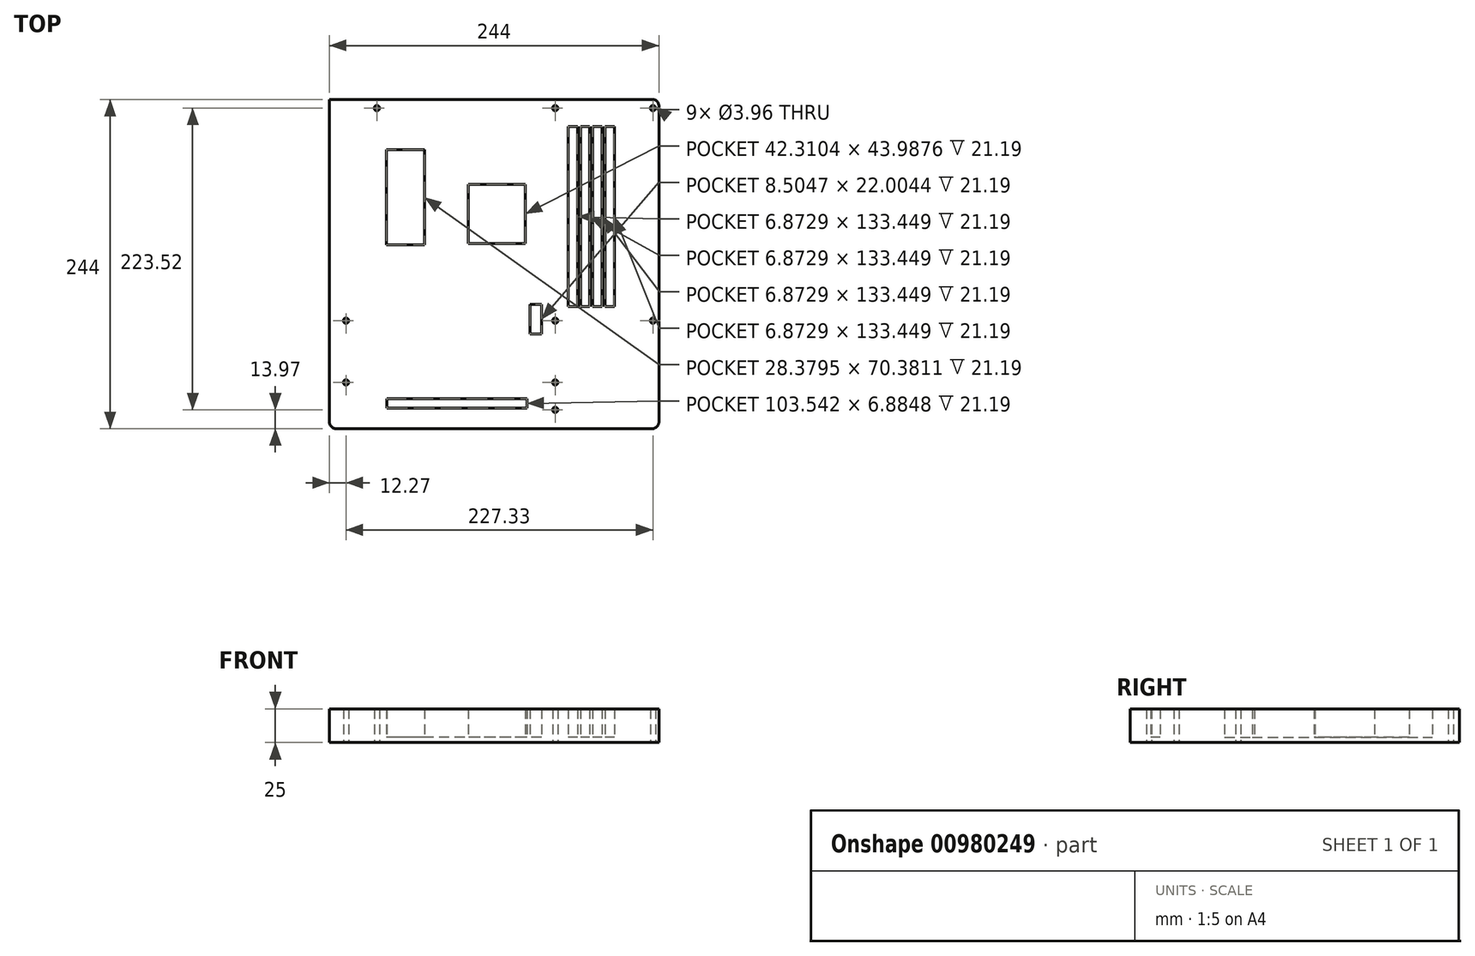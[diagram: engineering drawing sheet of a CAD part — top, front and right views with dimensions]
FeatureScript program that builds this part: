
annotation { "Feature Type Name" : "Feature", "Feature Type Description" : "" }
export const myFeature = defineFeature(function(context is Context, id is Id, definition is map)
    precondition{}
    {
        {
            var Q0;
            Q0=qCreatedBy(makeId("Top.planeOp"),FACE);
            var sketch = newSketch(context, id + "F0", { "sketchPlane" : qUnion([Q0])});
            skLineSegment(sketch, "E0.bottom", {"start": v(5, 0) * mm, "end": v(239, 0) * mm});
            skLineSegment(sketch, "E0.top", {"start": v(0, 244) * mm, "end": v(239, 244) * mm});
            skLineSegment(sketch, "E0.left", {"start": v(0, 5) * mm, "end": v(0, 244) * mm});
            skLineSegment(sketch, "E0.right", {"start": v(244, 5) * mm, "end": v(244, 239) * mm});
            skCircle(sketch, "E1", {"center": v(35.13, 237.49) * mm, "radius": 1.98 * mm});
            skCircle(sketch, "E2", {"center": v(167.2, 237.49) * mm, "radius": 1.98 * mm});
            skCircle(sketch, "E3", {"center": v(239.6, 237.49) * mm, "radius": 1.98 * mm});
            skCircle(sketch, "E4", {"center": v(12.27, 80) * mm, "radius": 1.98 * mm});
            skCircle(sketch, "E5", {"center": v(167.21, 80) * mm, "radius": 1.98 * mm});
            skCircle(sketch, "E6", {"center": v(239.6, 80) * mm, "radius": 1.98 * mm});
            skCircle(sketch, "E7", {"center": v(12.27, 34.3) * mm, "radius": 1.98 * mm});
            skCircle(sketch, "E8", {"center": v(167.21, 34.29) * mm, "radius": 1.98 * mm});
            skCircle(sketch, "E9", {"center": v(167.21, 13.97) * mm, "radius": 1.98 * mm});
            skLineSegment(sketch, "E10.bottom", {"start": v(0, 244) * mm, "end": v(22.47, 244) * mm});
            skLineSegment(sketch, "E10.top", {"start": v(0, 85.25) * mm, "end": v(22.47, 85.25) * mm});
            skLineSegment(sketch, "E10.left", {"start": v(0, 244) * mm, "end": v(0, 85.25) * mm});
            skLineSegment(sketch, "E10.right", {"start": v(22.47, 244) * mm, "end": v(22.47, 85.25) * mm});
            skLineSegment(sketch, "E11.bottom", {"start": v(148.54, 92.04) * mm, "end": v(157.04, 92.04) * mm});
            skLineSegment(sketch, "E11.top", {"start": v(148.54, 70.03) * mm, "end": v(157.04, 70.03) * mm});
            skLineSegment(sketch, "E11.left", {"start": v(148.54, 92.04) * mm, "end": v(148.54, 70.03) * mm});
            skLineSegment(sketch, "E11.right", {"start": v(157.04, 92.04) * mm, "end": v(157.04, 70.03) * mm});
            skLineSegment(sketch, "E12.bottom", {"start": v(102.72, 137.02) * mm, "end": v(145.03, 137.02) * mm});
            skLineSegment(sketch, "E12.top", {"start": v(102.72, 181) * mm, "end": v(145.03, 181) * mm});
            skLineSegment(sketch, "E12.left", {"start": v(102.72, 137.02) * mm, "end": v(102.72, 181) * mm});
            skLineSegment(sketch, "E12.right", {"start": v(145.03, 137.02) * mm, "end": v(145.03, 181) * mm});
            skLineSegment(sketch, "E13.bottom", {"start": v(176.77, 223.94) * mm, "end": v(183.64, 223.94) * mm});
            skLineSegment(sketch, "E13.top", {"start": v(176.77, 90.5) * mm, "end": v(183.64, 90.5) * mm});
            skLineSegment(sketch, "E13.left", {"start": v(176.77, 223.94) * mm, "end": v(176.77, 90.5) * mm});
            skLineSegment(sketch, "E13.right", {"start": v(183.64, 223.94) * mm, "end": v(183.64, 90.5) * mm});
            skLineSegment(sketch, "E14.1.0.0", {"start": v(192.74, 223.94) * mm, "end": v(192.74, 90.5) * mm});
            skLineSegment(sketch, "E14.1.0.1", {"start": v(185.87, 223.94) * mm, "end": v(185.87, 90.5) * mm});
            skLineSegment(sketch, "E14.1.0.2", {"start": v(185.87, 90.5) * mm, "end": v(192.74, 90.5) * mm});
            skLineSegment(sketch, "E14.1.0.3", {"start": v(185.87, 223.94) * mm, "end": v(192.74, 223.94) * mm});
            skLineSegment(sketch, "E14.2.0.0", {"start": v(201.84, 223.94) * mm, "end": v(201.84, 90.5) * mm});
            skLineSegment(sketch, "E14.2.0.1", {"start": v(194.97, 223.94) * mm, "end": v(194.97, 90.5) * mm});
            skLineSegment(sketch, "E14.2.0.2", {"start": v(194.97, 90.5) * mm, "end": v(201.84, 90.5) * mm});
            skLineSegment(sketch, "E14.2.0.3", {"start": v(194.97, 223.94) * mm, "end": v(201.84, 223.94) * mm});
            skLineSegment(sketch, "E14.3.0.0", {"start": v(210.94, 223.94) * mm, "end": v(210.94, 90.5) * mm});
            skLineSegment(sketch, "E14.3.0.1", {"start": v(204.07, 223.94) * mm, "end": v(204.07, 90.5) * mm});
            skLineSegment(sketch, "E14.3.0.2", {"start": v(204.07, 90.5) * mm, "end": v(210.94, 90.5) * mm});
            skLineSegment(sketch, "E14.3.0.3", {"start": v(204.07, 223.94) * mm, "end": v(210.94, 223.94) * mm});
            skLineSegment(sketch, "E14.direction1", {"start": v(183.64, 90.5) * mm, "end": v(192.74, 90.5) * mm, "construction": true});
            skLineSegment(sketch, "E15.bottom", {"start": v(42.63, 15.38) * mm, "end": v(146.17, 15.38) * mm});
            skLineSegment(sketch, "E15.top", {"start": v(42.63, 22.27) * mm, "end": v(146.17, 22.27) * mm});
            skLineSegment(sketch, "E15.left", {"start": v(42.63, 15.38) * mm, "end": v(42.63, 22.27) * mm});
            skLineSegment(sketch, "E15.right", {"start": v(146.17, 15.38) * mm, "end": v(146.17, 22.27) * mm});
            skLineSegment(sketch, "E16.bottom", {"start": v(42.19, 136.37) * mm, "end": v(70.57, 136.37) * mm});
            skLineSegment(sketch, "E16.top", {"start": v(42.19, 206.75) * mm, "end": v(70.57, 206.75) * mm});
            skLineSegment(sketch, "E16.left", {"start": v(42.19, 136.37) * mm, "end": v(42.19, 206.75) * mm});
            skLineSegment(sketch, "E16.right", {"start": v(70.57, 136.37) * mm, "end": v(70.57, 206.75) * mm});
            skLineSegment(sketch, "E17.bottom", {"start": v(85.1, 221.74) * mm, "end": v(155.48, 221.74) * mm});
            skLineSegment(sketch, "E17.top", {"start": v(85.1, 244) * mm, "end": v(155.48, 244) * mm});
            skLineSegment(sketch, "E17.left", {"start": v(85.1, 221.74) * mm, "end": v(85.1, 244) * mm});
            skLineSegment(sketch, "E17.right", {"start": v(155.48, 221.74) * mm, "end": v(155.48, 244) * mm});
            skPoint(sketch, "E18.visualSharp", {"position": v(244, 0) * mm});
            skArc(sketch, "E18.filletArc", {"start": v(239, 0) * mm, "mid": v(242.54, 1.46) * mm, "end": v(244, 5) * mm});
            skPoint(sketch, "E19.visualSharp", {"position": v(244, 244) * mm});
            skArc(sketch, "E19.filletArc", {"start": v(244, 239) * mm, "mid": v(242.54, 242.54) * mm, "end": v(239, 244) * mm});
            skPoint(sketch, "E20.visualSharp", {"position": v(0, 0) * mm});
            skArc(sketch, "E20.filletArc", {"start": v(0, 5) * mm, "mid": v(1.46, 1.46) * mm, "end": v(5, 0) * mm});
            skSolve(sketch);
        }
        {
            var Q0;
            Q0=makeQuery(id+"F0.imprint","IMPRINT",FACE,{"disambiguationData":[TD([[makeQuery(id+"F0.imprint","IMPRINT",EDGE,{"derivedFrom":sQuery(id+"F0.wireOp",EDGE,"E0.bottom")}),1.0]])]});
            var Q1;
            Q1=makeQuery(id+"F0.imprint","IMPRINT",FACE,{"disambiguationData":[TD([[makeQuery(id+"F0.imprint","IMPRINT",EDGE,{"derivedFrom":sQuery(id+"F0.wireOp",EDGE,"E15.bottom")}),1.0]])]});
            var Q2;
            Q2=makeQuery(id+"F0.imprint","IMPRINT",FACE,{"disambiguationData":[TD([[makeQuery(id+"F0.imprint","IMPRINT",EDGE,{"derivedFrom":sQuery(id+"F0.wireOp",EDGE,"E11.bottom")}),-1.0]])]});
            var Q3;
            Q3=makeQuery(id+"F0.imprint","IMPRINT",FACE,{"disambiguationData":[TD([[makeQuery(id+"F0.imprint","IMPRINT",EDGE,{"derivedFrom":sQuery(id+"F0.wireOp",EDGE,"E13.bottom")}),-1.0]])]});
            var Q4;
            Q4=makeQuery(id+"F0.imprint","IMPRINT",FACE,{"disambiguationData":[TD([[makeQuery(id+"F0.imprint","IMPRINT",EDGE,{"derivedFrom":sQuery(id+"F0.wireOp",EDGE,"E14.1.0.0")}),-1.0]])]});
            var Q5;
            Q5=makeQuery(id+"F0.imprint","IMPRINT",FACE,{"disambiguationData":[TD([[makeQuery(id+"F0.imprint","IMPRINT",EDGE,{"derivedFrom":sQuery(id+"F0.wireOp",EDGE,"E14.2.0.0")}),-1.0]])]});
            var Q6;
            Q6=makeQuery(id+"F0.imprint","IMPRINT",FACE,{"disambiguationData":[TD([[makeQuery(id+"F0.imprint","IMPRINT",EDGE,{"derivedFrom":sQuery(id+"F0.wireOp",EDGE,"E14.3.0.0")}),-1.0]])]});
            var Q7;
            Q7=makeQuery(id+"F0.imprint","IMPRINT",FACE,{"disambiguationData":[TD([[makeQuery(id+"F0.imprint","IMPRINT",EDGE,{"derivedFrom":sQuery(id+"F0.wireOp",EDGE,"E12.bottom")}),1.0]])]});
            var Q8;
            Q8=makeQuery(id+"F0.imprint","IMPRINT",FACE,{"disambiguationData":[TD([[makeQuery(id+"F0.imprint","IMPRINT",EDGE,{"derivedFrom":sQuery(id+"F0.wireOp",EDGE,"E16.bottom")}),1.0]])]});
            var Q9;
            Q9=makeQuery(id+"F0.imprint","IMPRINT",FACE,{"disambiguationData":[TD([[makeQuery(id+"F0.imprint","IMPRINT",EDGE,{"derivedFrom":sQuery(id+"F0.wireOp",EDGE,"E17.bottom")}),1.0]])]});
            var Q10;
            {var subQ4=sQuery(id+"F0.wireOp",EDGE,"E10.top");Q10=makeQuery(id+"F0.imprint","IMPRINT",FACE,{"disambiguationData":[TD([[makeQuery(id+"F0.imprint","IMPRINT",EDGE,{"derivedFrom":subQ4}),1.0]])]});}
            extrude(context, id + "F1", {"entities" : qUnion([Q0, Q1, Q2, Q3, Q4, Q5, Q6, Q7, Q8, Q9, Q10]), "depth" : 3.81 * mm, "offsetDistance" : 25 * mm});
        }
        {
            var Q0;
            {var subQ4=sQuery(id+"F0.wireOp",EDGE,"E10.top");var subQ12=makeQuery(id+"F0.imprint","IMPRINT",EDGE,{"derivedFrom":subQ4});var subQ14=makeQuery(id+"F0.imprint","IMPRINT",EDGE,{"derivedFrom":sQuery(id+"F0.wireOp",EDGE,"E17.bottom")});Q0=qUnion([makeQuery(id+"F0.imprint","IMPRINT",FACE,{"disambiguationData":[TD([[subQ14,1.0]])]}),makeQuery(id+"F0.imprint","IMPRINT",FACE,{"disambiguationData":[TD([[subQ12,1.0]])]}),makeQuery(id+"F0.imprint","IMPRINT",FACE,{"disambiguationData":[TD([[makeQuery(id+"F0.imprint","IMPRINT",EDGE,{"derivedFrom":sQuery(id+"F0.wireOp",EDGE,"E0.bottom")}),1.0]])]})]);}
            extrude(context, id + "F2", {"entities" : qUnion([Q0]), "operationType" : NewBodyOperationType.ADD, "depth" : 25 * mm, "offsetDistance" : 25 * mm});
        }
    });
